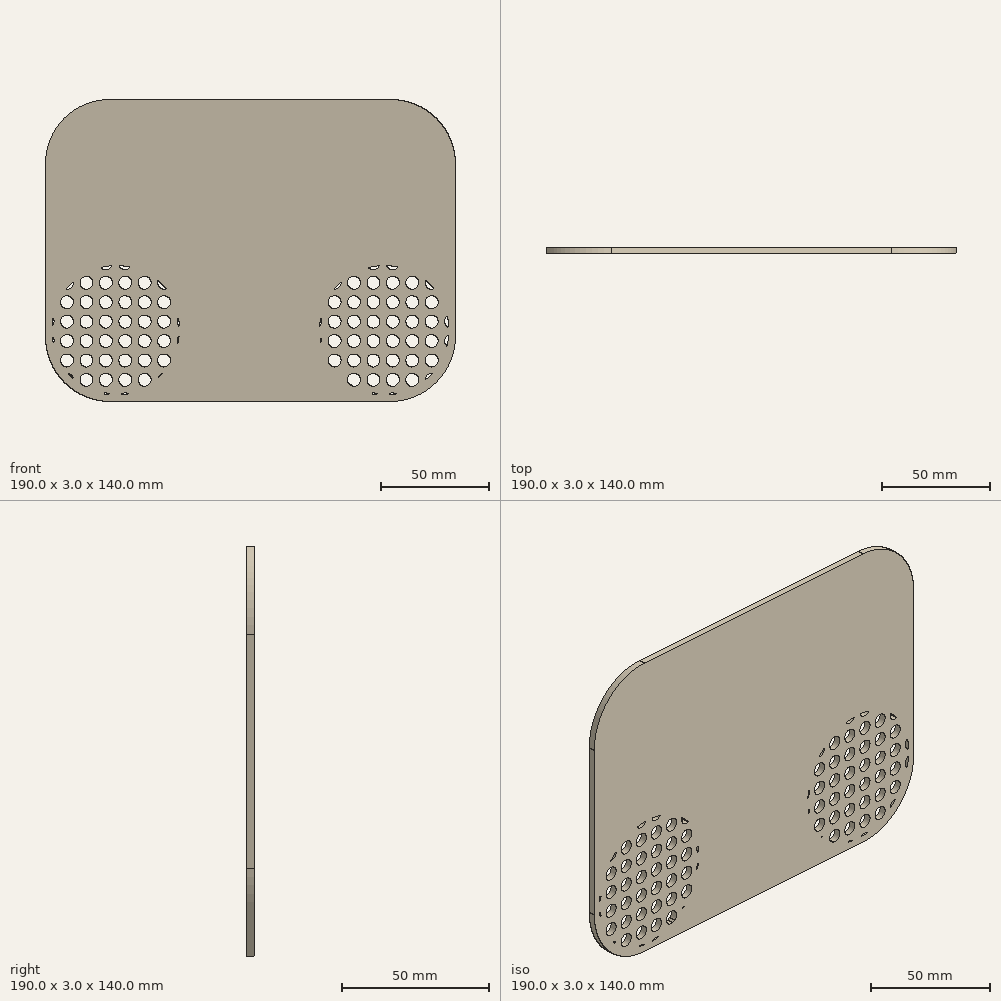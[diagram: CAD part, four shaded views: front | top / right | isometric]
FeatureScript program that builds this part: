
annotation { "Feature Type Name" : "Feature", "Feature Type Description" : "" }
export const myFeature = defineFeature(function(context is Context, id is Id, definition is map)
    precondition{}
    {
        {
            var Q0;
            Q0=qCreatedBy(makeId("Front.planeOp"),FACE);
            var sketch = newSketch(context, id + "F0", { "sketchPlane" : qUnion([Q0])});
            skArc(sketch, "E0", {"start": v(41.98, -14.66) * mm, "mid": v(40.32, -16.26) * mm, "end": v(38.79, -18) * mm});
            skArc(sketch, "E1", {"start": v(32.53, -31.39) * mm, "mid": v(32.23, -33.28) * mm, "end": v(32.05, -35.19) * mm});
            skArc(sketch, "E2", {"start": v(32.1, -39.4) * mm, "mid": v(32.32, -41.38) * mm, "end": v(32.68, -43.35) * mm});
            skArc(sketch, "E3", {"start": v(39.72, -57.09) * mm, "mid": v(40.79, -58.21) * mm, "end": v(41.91, -59.28) * mm});
            skArc(sketch, "E4", {"start": v(55.65, -66.32) * mm, "mid": v(57.37, -66.64) * mm, "end": v(59.1, -66.86) * mm});
            skArc(sketch, "E5", {"start": v(63.81, -66.95) * mm, "mid": v(65.72, -66.77) * mm, "end": v(67.61, -66.47) * mm});
            skArc(sketch, "E6", {"start": v(81, -60.21) * mm, "mid": v(82.74, -58.68) * mm, "end": v(84.34, -57.02) * mm});
            skArc(sketch, "E7", {"start": v(91.1, -44.32) * mm, "mid": v(91.62, -41.78) * mm, "end": v(91.92, -39.2) * mm});
            skArc(sketch, "E8", {"start": v(91.98, -35.82) * mm, "mid": v(91.75, -33.16) * mm, "end": v(91.3, -30.53) * mm});
            skArc(sketch, "E9", {"start": v(85.06, -17.8) * mm, "mid": v(83.21, -15.79) * mm, "end": v(81.2, -13.94) * mm});
            skArc(sketch, "E10", {"start": v(68.47, -7.7) * mm, "mid": v(65.84, -7.25) * mm, "end": v(63.18, -7.02) * mm});
            skArc(sketch, "E11", {"start": v(59.8, -7.08) * mm, "mid": v(57.22, -7.38) * mm, "end": v(54.68, -7.9) * mm});
            skLineSegment(sketch, "E12", {"start": v(-65, -70) * mm, "end": v(65, -70) * mm});
            skLineSegment(sketch, "E13", {"start": v(95, -40) * mm, "end": v(95, 40) * mm});
            skLineSegment(sketch, "E14", {"start": v(65, 70) * mm, "end": v(-65, 70) * mm});
            skLineSegment(sketch, "E15", {"start": v(-95, 40) * mm, "end": v(-95, -40) * mm});
            skArc(sketch, "E16", {"start": v(-65, 70) * mm, "mid": v(-86.21, 61.21) * mm, "end": v(-95, 40) * mm});
            skArc(sketch, "E17", {"start": v(-95, -40) * mm, "mid": v(-86.21, -61.21) * mm, "end": v(-65, -70) * mm});
            skArc(sketch, "E18", {"start": v(95, 40) * mm, "mid": v(86.21, 61.21) * mm, "end": v(65, 70) * mm});
            skArc(sketch, "E19", {"start": v(65, -70) * mm, "mid": v(86.21, -61.21) * mm, "end": v(95, -40) * mm});
            skArc(sketch, "E20", {"start": v(59.1, -66.86) * mm, "mid": v(57.46, -66.04) * mm, "end": v(55.65, -66.32) * mm});
            skArc(sketch, "E21", {"start": v(67.61, -66.47) * mm, "mid": v(65.63, -66.02) * mm, "end": v(63.81, -66.95) * mm});
            skArc(sketch, "E22", {"start": v(41.91, -59.28) * mm, "mid": v(41.12, -57.88) * mm, "end": v(39.72, -57.09) * mm});
            skCircle(sketch, "E23", {"center": v(48, -60) * mm, "radius": 3 * mm});
            skCircle(sketch, "E24", {"center": v(57, -60) * mm, "radius": 3 * mm});
            skCircle(sketch, "E25", {"center": v(66, -60) * mm, "radius": 3 * mm});
            skCircle(sketch, "E26", {"center": v(75, -60) * mm, "radius": 3 * mm});
            skArc(sketch, "E27", {"start": v(84.34, -57.02) * mm, "mid": v(81.93, -57.83) * mm, "end": v(81, -60.21) * mm});
            skCircle(sketch, "E28", {"center": v(39, -51) * mm, "radius": 3 * mm});
            skCircle(sketch, "E29", {"center": v(48, -51) * mm, "radius": 3 * mm});
            skCircle(sketch, "E30", {"center": v(57, -51) * mm, "radius": 3 * mm});
            skCircle(sketch, "E31", {"center": v(66, -51) * mm, "radius": 3 * mm});
            skCircle(sketch, "E32", {"center": v(75, -51) * mm, "radius": 3 * mm});
            skCircle(sketch, "E33", {"center": v(84, -51) * mm, "radius": 3 * mm});
            skArc(sketch, "E34", {"start": v(32.68, -43.35) * mm, "mid": v(32.96, -41.54) * mm, "end": v(32.14, -39.9) * mm});
            skCircle(sketch, "E35", {"center": v(39, -42) * mm, "radius": 3 * mm});
            skCircle(sketch, "E36", {"center": v(48, -42) * mm, "radius": 3 * mm});
            skCircle(sketch, "E37", {"center": v(57, -42) * mm, "radius": 3 * mm});
            skCircle(sketch, "E38", {"center": v(66, -42) * mm, "radius": 3 * mm});
            skCircle(sketch, "E39", {"center": v(75, -42) * mm, "radius": 3 * mm});
            skCircle(sketch, "E40", {"center": v(84, -42) * mm, "radius": 3 * mm});
            skArc(sketch, "E41", {"start": v(91.92, -39.2) * mm, "mid": v(90.04, -41.52) * mm, "end": v(91.1, -44.32) * mm});
            skArc(sketch, "E42", {"start": v(32.05, -35.19) * mm, "mid": v(32.98, -33.37) * mm, "end": v(32.53, -31.39) * mm});
            skCircle(sketch, "E43", {"center": v(39, -33) * mm, "radius": 3 * mm});
            skCircle(sketch, "E44", {"center": v(48, -33) * mm, "radius": 3 * mm});
            skCircle(sketch, "E45", {"center": v(57, -33) * mm, "radius": 3 * mm});
            skCircle(sketch, "E46", {"center": v(66, -33) * mm, "radius": 3 * mm});
            skCircle(sketch, "E47", {"center": v(75, -33) * mm, "radius": 3 * mm});
            skCircle(sketch, "E48", {"center": v(84, -33) * mm, "radius": 3 * mm});
            skArc(sketch, "E49", {"start": v(91.3, -30.53) * mm, "mid": v(90.02, -33.38) * mm, "end": v(91.98, -35.82) * mm});
            skCircle(sketch, "E50", {"center": v(39, -24) * mm, "radius": 3 * mm});
            skCircle(sketch, "E51", {"center": v(48, -24) * mm, "radius": 3 * mm});
            skCircle(sketch, "E52", {"center": v(57, -24) * mm, "radius": 3 * mm});
            skCircle(sketch, "E53", {"center": v(66, -24) * mm, "radius": 3 * mm});
            skCircle(sketch, "E54", {"center": v(75, -24) * mm, "radius": 3 * mm});
            skCircle(sketch, "E55", {"center": v(84, -24) * mm, "radius": 3 * mm});
            skArc(sketch, "E56", {"start": v(38.79, -18) * mm, "mid": v(41.17, -17.07) * mm, "end": v(41.98, -14.66) * mm});
            skCircle(sketch, "E57", {"center": v(48, -15) * mm, "radius": 3 * mm});
            skCircle(sketch, "E58", {"center": v(57, -15) * mm, "radius": 3 * mm});
            skCircle(sketch, "E59", {"center": v(66, -15) * mm, "radius": 3 * mm});
            skCircle(sketch, "E60", {"center": v(75, -15) * mm, "radius": 3 * mm});
            skArc(sketch, "E61", {"start": v(81.2, -13.94) * mm, "mid": v(81.88, -17.12) * mm, "end": v(85.06, -17.8) * mm});
            skArc(sketch, "E62", {"start": v(54.68, -7.9) * mm, "mid": v(57.48, -8.96) * mm, "end": v(59.8, -7.08) * mm});
            skArc(sketch, "E63", {"start": v(63.18, -7.02) * mm, "mid": v(65.62, -8.98) * mm, "end": v(68.47, -7.7) * mm});
            skArc(sketch, "E64", {"start": v(-84.28, -57.09) * mm, "mid": v(-83.21, -58.21) * mm, "end": v(-82.09, -59.28) * mm});
            skArc(sketch, "E65", {"start": v(-68.35, -66.32) * mm, "mid": v(-66.63, -66.64) * mm, "end": v(-64.9, -66.86) * mm});
            skArc(sketch, "E66", {"start": v(-60.19, -66.95) * mm, "mid": v(-58.28, -66.77) * mm, "end": v(-56.39, -66.47) * mm});
            skArc(sketch, "E67", {"start": v(-43.03, -60.24) * mm, "mid": v(-41.28, -58.7) * mm, "end": v(-39.66, -57.02) * mm});
            skArc(sketch, "E68", {"start": v(-32.9, -44.32) * mm, "mid": v(-32.38, -41.78) * mm, "end": v(-32.08, -39.2) * mm});
            skArc(sketch, "E69", {"start": v(-32.02, -35.82) * mm, "mid": v(-32.25, -33.16) * mm, "end": v(-32.7, -30.53) * mm});
            skArc(sketch, "E70", {"start": v(-38.94, -17.8) * mm, "mid": v(-40.79, -15.79) * mm, "end": v(-42.8, -13.94) * mm});
            skArc(sketch, "E71", {"start": v(-55.53, -7.7) * mm, "mid": v(-58.16, -7.25) * mm, "end": v(-60.82, -7.02) * mm});
            skArc(sketch, "E72", {"start": v(-64.2, -7.08) * mm, "mid": v(-66.78, -7.38) * mm, "end": v(-69.32, -7.9) * mm});
            skArc(sketch, "E73", {"start": v(-82.02, -14.66) * mm, "mid": v(-83.68, -16.26) * mm, "end": v(-85.21, -18) * mm});
            skArc(sketch, "E74", {"start": v(-91.47, -31.39) * mm, "mid": v(-91.77, -33.28) * mm, "end": v(-91.95, -35.19) * mm});
            skArc(sketch, "E75", {"start": v(-91.86, -39.9) * mm, "mid": v(-91.64, -41.63) * mm, "end": v(-91.32, -43.35) * mm});
            skArc(sketch, "E76", {"start": v(-64.9, -66.86) * mm, "mid": v(-66.54, -66.04) * mm, "end": v(-68.35, -66.32) * mm});
            skArc(sketch, "E77", {"start": v(-56.39, -66.47) * mm, "mid": v(-58.37, -66.02) * mm, "end": v(-60.19, -66.95) * mm});
            skArc(sketch, "E78", {"start": v(-82.09, -59.28) * mm, "mid": v(-82.88, -57.88) * mm, "end": v(-84.28, -57.09) * mm});
            skCircle(sketch, "E79", {"center": v(-76, -60) * mm, "radius": 3 * mm});
            skCircle(sketch, "E80", {"center": v(-67, -60) * mm, "radius": 3 * mm});
            skCircle(sketch, "E81", {"center": v(-58, -60) * mm, "radius": 3 * mm});
            skCircle(sketch, "E82", {"center": v(-49, -60) * mm, "radius": 3 * mm});
            skArc(sketch, "E83", {"start": v(-39.66, -57.02) * mm, "mid": v(-42.07, -57.83) * mm, "end": v(-43, -60.21) * mm});
            skCircle(sketch, "E84", {"center": v(-85, -51) * mm, "radius": 3 * mm});
            skCircle(sketch, "E85", {"center": v(-76, -51) * mm, "radius": 3 * mm});
            skCircle(sketch, "E86", {"center": v(-67, -51) * mm, "radius": 3 * mm});
            skCircle(sketch, "E87", {"center": v(-58, -51) * mm, "radius": 3 * mm});
            skCircle(sketch, "E88", {"center": v(-49, -51) * mm, "radius": 3 * mm});
            skCircle(sketch, "E89", {"center": v(-40, -51) * mm, "radius": 3 * mm});
            skArc(sketch, "E90", {"start": v(-91.32, -43.35) * mm, "mid": v(-91.04, -41.54) * mm, "end": v(-91.86, -39.9) * mm});
            skCircle(sketch, "E91", {"center": v(-85, -42) * mm, "radius": 3 * mm});
            skCircle(sketch, "E92", {"center": v(-76, -42) * mm, "radius": 3 * mm});
            skCircle(sketch, "E93", {"center": v(-67, -42) * mm, "radius": 3 * mm});
            skCircle(sketch, "E94", {"center": v(-58, -42) * mm, "radius": 3 * mm});
            skCircle(sketch, "E95", {"center": v(-49, -42) * mm, "radius": 3 * mm});
            skCircle(sketch, "E96", {"center": v(-40, -42) * mm, "radius": 3 * mm});
            skArc(sketch, "E97", {"start": v(-32.08, -39.2) * mm, "mid": v(-33.96, -41.52) * mm, "end": v(-32.9, -44.32) * mm});
            skArc(sketch, "E98", {"start": v(-91.95, -35.19) * mm, "mid": v(-91.02, -33.37) * mm, "end": v(-91.47, -31.39) * mm});
            skCircle(sketch, "E99", {"center": v(-85, -33) * mm, "radius": 3 * mm});
            skCircle(sketch, "E100", {"center": v(-76, -33) * mm, "radius": 3 * mm});
            skCircle(sketch, "E101", {"center": v(-67, -33) * mm, "radius": 3 * mm});
            skCircle(sketch, "E102", {"center": v(-58, -33) * mm, "radius": 3 * mm});
            skCircle(sketch, "E103", {"center": v(-49, -33) * mm, "radius": 3 * mm});
            skCircle(sketch, "E104", {"center": v(-40, -33) * mm, "radius": 3 * mm});
            skArc(sketch, "E105", {"start": v(-32.7, -30.53) * mm, "mid": v(-33.98, -33.38) * mm, "end": v(-32.02, -35.82) * mm});
            skCircle(sketch, "E106", {"center": v(-85, -24) * mm, "radius": 3 * mm});
            skCircle(sketch, "E107", {"center": v(-76, -24) * mm, "radius": 3 * mm});
            skCircle(sketch, "E108", {"center": v(-67, -24) * mm, "radius": 3 * mm});
            skCircle(sketch, "E109", {"center": v(-58, -24) * mm, "radius": 3 * mm});
            skCircle(sketch, "E110", {"center": v(-49, -24) * mm, "radius": 3 * mm});
            skCircle(sketch, "E111", {"center": v(-40, -24) * mm, "radius": 3 * mm});
            skArc(sketch, "E112", {"start": v(-85.21, -18) * mm, "mid": v(-82.83, -17.07) * mm, "end": v(-82.02, -14.66) * mm});
            skCircle(sketch, "E113", {"center": v(-76, -15) * mm, "radius": 3 * mm});
            skCircle(sketch, "E114", {"center": v(-67, -15) * mm, "radius": 3 * mm});
            skCircle(sketch, "E115", {"center": v(-58, -15) * mm, "radius": 3 * mm});
            skCircle(sketch, "E116", {"center": v(-49, -15) * mm, "radius": 3 * mm});
            skArc(sketch, "E117", {"start": v(-42.8, -13.94) * mm, "mid": v(-42.12, -17.12) * mm, "end": v(-38.94, -17.8) * mm});
            skArc(sketch, "E118", {"start": v(-69.32, -7.9) * mm, "mid": v(-66.52, -8.96) * mm, "end": v(-64.2, -7.08) * mm});
            skArc(sketch, "E119", {"start": v(-60.82, -7.02) * mm, "mid": v(-58.38, -8.98) * mm, "end": v(-55.53, -7.7) * mm});
            skSolve(sketch);
        }
        {
            var Q0;
            Q0 = qSketchRegion(id + "F0", true);
            extrude(context, id + "F1", {"entities" : qUnion([Q0]), "depth" : 3 * mm});
        }
        {
            var Q0;
            Q0=makeQuery(id+"F1.opExtrude","CAP_FACE",FACE,{"disambiguationData":[OSD([sQuery(id+"F0.wireOp",EDGE,"E0"),sQuery(id+"F0.wireOp",EDGE,"E1"),sQuery(id+"F0.wireOp",EDGE,"E2"),sQuery(id+"F0.wireOp",EDGE,"E3"),sQuery(id+"F0.wireOp",EDGE,"E4"),sQuery(id+"F0.wireOp",EDGE,"E5"),sQuery(id+"F0.wireOp",EDGE,"E6"),sQuery(id+"F0.wireOp",EDGE,"E7"),sQuery(id+"F0.wireOp",EDGE,"E8"),sQuery(id+"F0.wireOp",EDGE,"E9"),sQuery(id+"F0.wireOp",EDGE,"E10"),sQuery(id+"F0.wireOp",EDGE,"E11"),sQuery(id+"F0.wireOp",EDGE,"E12"),sQuery(id+"F0.wireOp",EDGE,"E13"),sQuery(id+"F0.wireOp",EDGE,"E14"),sQuery(id+"F0.wireOp",EDGE,"E15"),sQuery(id+"F0.wireOp",EDGE,"E16"),sQuery(id+"F0.wireOp",EDGE,"E17"),sQuery(id+"F0.wireOp",EDGE,"E18"),sQuery(id+"F0.wireOp",EDGE,"E19"),sQuery(id+"F0.wireOp",EDGE,"E20"),sQuery(id+"F0.wireOp",EDGE,"E21"),sQuery(id+"F0.wireOp",EDGE,"E22"),sQuery(id+"F0.wireOp",EDGE,"E23"),sQuery(id+"F0.wireOp",EDGE,"E24"),sQuery(id+"F0.wireOp",EDGE,"E25"),sQuery(id+"F0.wireOp",EDGE,"E26"),sQuery(id+"F0.wireOp",EDGE,"E27"),sQuery(id+"F0.wireOp",EDGE,"E28"),sQuery(id+"F0.wireOp",EDGE,"E29"),sQuery(id+"F0.wireOp",EDGE,"E30"),sQuery(id+"F0.wireOp",EDGE,"E31"),sQuery(id+"F0.wireOp",EDGE,"E32"),sQuery(id+"F0.wireOp",EDGE,"E33"),sQuery(id+"F0.wireOp",EDGE,"E34"),sQuery(id+"F0.wireOp",EDGE,"E35"),sQuery(id+"F0.wireOp",EDGE,"E36"),sQuery(id+"F0.wireOp",EDGE,"E37"),sQuery(id+"F0.wireOp",EDGE,"E38"),sQuery(id+"F0.wireOp",EDGE,"E39"),sQuery(id+"F0.wireOp",EDGE,"E40"),sQuery(id+"F0.wireOp",EDGE,"E41"),sQuery(id+"F0.wireOp",EDGE,"E42"),sQuery(id+"F0.wireOp",EDGE,"E43"),sQuery(id+"F0.wireOp",EDGE,"E44"),sQuery(id+"F0.wireOp",EDGE,"E45"),sQuery(id+"F0.wireOp",EDGE,"E46"),sQuery(id+"F0.wireOp",EDGE,"E47"),sQuery(id+"F0.wireOp",EDGE,"E48"),sQuery(id+"F0.wireOp",EDGE,"E49"),sQuery(id+"F0.wireOp",EDGE,"E50"),sQuery(id+"F0.wireOp",EDGE,"E51"),sQuery(id+"F0.wireOp",EDGE,"E52"),sQuery(id+"F0.wireOp",EDGE,"E53"),sQuery(id+"F0.wireOp",EDGE,"E54"),sQuery(id+"F0.wireOp",EDGE,"E55"),sQuery(id+"F0.wireOp",EDGE,"E56"),sQuery(id+"F0.wireOp",EDGE,"E57"),sQuery(id+"F0.wireOp",EDGE,"E58"),sQuery(id+"F0.wireOp",EDGE,"E59"),sQuery(id+"F0.wireOp",EDGE,"E60"),sQuery(id+"F0.wireOp",EDGE,"E61"),sQuery(id+"F0.wireOp",EDGE,"E62"),sQuery(id+"F0.wireOp",EDGE,"E63"),sQuery(id+"F0.wireOp",EDGE,"E64"),sQuery(id+"F0.wireOp",EDGE,"E65"),sQuery(id+"F0.wireOp",EDGE,"E66"),sQuery(id+"F0.wireOp",EDGE,"E67"),sQuery(id+"F0.wireOp",EDGE,"E68"),sQuery(id+"F0.wireOp",EDGE,"E69"),sQuery(id+"F0.wireOp",EDGE,"E70"),sQuery(id+"F0.wireOp",EDGE,"E71"),sQuery(id+"F0.wireOp",EDGE,"E72"),sQuery(id+"F0.wireOp",EDGE,"E73"),sQuery(id+"F0.wireOp",EDGE,"E74"),sQuery(id+"F0.wireOp",EDGE,"E75"),sQuery(id+"F0.wireOp",EDGE,"E76"),sQuery(id+"F0.wireOp",EDGE,"E77"),sQuery(id+"F0.wireOp",EDGE,"E78"),sQuery(id+"F0.wireOp",EDGE,"E79"),sQuery(id+"F0.wireOp",EDGE,"E80"),sQuery(id+"F0.wireOp",EDGE,"E81"),sQuery(id+"F0.wireOp",EDGE,"E82"),sQuery(id+"F0.wireOp",EDGE,"E83"),sQuery(id+"F0.wireOp",EDGE,"E84"),sQuery(id+"F0.wireOp",EDGE,"E85"),sQuery(id+"F0.wireOp",EDGE,"E86"),sQuery(id+"F0.wireOp",EDGE,"E87"),sQuery(id+"F0.wireOp",EDGE,"E88"),sQuery(id+"F0.wireOp",EDGE,"E89"),sQuery(id+"F0.wireOp",EDGE,"E90"),sQuery(id+"F0.wireOp",EDGE,"E91"),sQuery(id+"F0.wireOp",EDGE,"E92"),sQuery(id+"F0.wireOp",EDGE,"E93"),sQuery(id+"F0.wireOp",EDGE,"E94"),sQuery(id+"F0.wireOp",EDGE,"E95"),sQuery(id+"F0.wireOp",EDGE,"E96"),sQuery(id+"F0.wireOp",EDGE,"E97"),sQuery(id+"F0.wireOp",EDGE,"E98"),sQuery(id+"F0.wireOp",EDGE,"E99"),sQuery(id+"F0.wireOp",EDGE,"E100"),sQuery(id+"F0.wireOp",EDGE,"E101"),sQuery(id+"F0.wireOp",EDGE,"E102"),sQuery(id+"F0.wireOp",EDGE,"E103"),sQuery(id+"F0.wireOp",EDGE,"E104"),sQuery(id+"F0.wireOp",EDGE,"E105"),sQuery(id+"F0.wireOp",EDGE,"E106"),sQuery(id+"F0.wireOp",EDGE,"E107"),sQuery(id+"F0.wireOp",EDGE,"E108"),sQuery(id+"F0.wireOp",EDGE,"E109"),sQuery(id+"F0.wireOp",EDGE,"E110"),sQuery(id+"F0.wireOp",EDGE,"E111"),sQuery(id+"F0.wireOp",EDGE,"E112"),sQuery(id+"F0.wireOp",EDGE,"E113"),sQuery(id+"F0.wireOp",EDGE,"E114"),sQuery(id+"F0.wireOp",EDGE,"E115"),sQuery(id+"F0.wireOp",EDGE,"E116"),sQuery(id+"F0.wireOp",EDGE,"E117"),sQuery(id+"F0.wireOp",EDGE,"E118"),sQuery(id+"F0.wireOp",EDGE,"E119")])],"isStart":false});
            var sketch = newSketch(context, id + "F2", { "sketchPlane" : qUnion([Q0])});
            skLineSegment(sketch, "E120", {"start": v(77.02, 48) * mm, "end": v(77.02, -10.74) * mm});
            skArc(sketch, "E121", {"start": v(77.02, -10.74) * mm, "mid": v(35.92, -21.87) * mm, "end": v(47.46, -62.85) * mm});
            skLineSegment(sketch, "E122", {"start": v(-48.07, -62.85) * mm, "end": v(47.46, -62.85) * mm});
            skArc(sketch, "E123", {"start": v(-48.07, -62.85) * mm, "mid": v(-34.84, -47.38) * mm, "end": v(-34.5, -27.03) * mm});
            skPoint(sketch, "E124.end.orphan", {"position": v(-31, -33) * mm});
            skLineSegment(sketch, "E125", {"start": v(72.26, 50.43) * mm, "end": v(-34.5, -27.03) * mm});
            skPoint(sketch, "E126.visualSharp", {"position": v(77.02, 53.88) * mm});
            skArc(sketch, "E126.filletArc", {"start": v(77.02, 48) * mm, "mid": v(75.38, 50.67) * mm, "end": v(72.26, 50.43) * mm});
            skSolve(sketch);
        }
        {
            var Q0;
            Q0 = qSketchRegion(id + "F2", true);
            extrude(context, id + "F3", {"entities" : qUnion([Q0]), "operationType" : NewBodyOperationType.ADD, "oppositeDirection" : true, "depth" : 3 * mm});
        }
        {
            var Q0;
            Q0=makeQuery(id+"F1.opExtrude","CAP_FACE",FACE,{"disambiguationData":[OSD([sQuery(id+"F0.wireOp",EDGE,"E0"),sQuery(id+"F0.wireOp",EDGE,"E1"),sQuery(id+"F0.wireOp",EDGE,"E2"),sQuery(id+"F0.wireOp",EDGE,"E3"),sQuery(id+"F0.wireOp",EDGE,"E4"),sQuery(id+"F0.wireOp",EDGE,"E5"),sQuery(id+"F0.wireOp",EDGE,"E6"),sQuery(id+"F0.wireOp",EDGE,"E7"),sQuery(id+"F0.wireOp",EDGE,"E8"),sQuery(id+"F0.wireOp",EDGE,"E9"),sQuery(id+"F0.wireOp",EDGE,"E10"),sQuery(id+"F0.wireOp",EDGE,"E11"),sQuery(id+"F0.wireOp",EDGE,"E12"),sQuery(id+"F0.wireOp",EDGE,"E13"),sQuery(id+"F0.wireOp",EDGE,"E14"),sQuery(id+"F0.wireOp",EDGE,"E15"),sQuery(id+"F0.wireOp",EDGE,"E16"),sQuery(id+"F0.wireOp",EDGE,"E17"),sQuery(id+"F0.wireOp",EDGE,"E18"),sQuery(id+"F0.wireOp",EDGE,"E19"),sQuery(id+"F0.wireOp",EDGE,"E20"),sQuery(id+"F0.wireOp",EDGE,"E21"),sQuery(id+"F0.wireOp",EDGE,"E22"),sQuery(id+"F0.wireOp",EDGE,"E23"),sQuery(id+"F0.wireOp",EDGE,"E24"),sQuery(id+"F0.wireOp",EDGE,"E25"),sQuery(id+"F0.wireOp",EDGE,"E26"),sQuery(id+"F0.wireOp",EDGE,"E27"),sQuery(id+"F0.wireOp",EDGE,"E28"),sQuery(id+"F0.wireOp",EDGE,"E29"),sQuery(id+"F0.wireOp",EDGE,"E30"),sQuery(id+"F0.wireOp",EDGE,"E31"),sQuery(id+"F0.wireOp",EDGE,"E32"),sQuery(id+"F0.wireOp",EDGE,"E33"),sQuery(id+"F0.wireOp",EDGE,"E34"),sQuery(id+"F0.wireOp",EDGE,"E35"),sQuery(id+"F0.wireOp",EDGE,"E36"),sQuery(id+"F0.wireOp",EDGE,"E37"),sQuery(id+"F0.wireOp",EDGE,"E38"),sQuery(id+"F0.wireOp",EDGE,"E39"),sQuery(id+"F0.wireOp",EDGE,"E40"),sQuery(id+"F0.wireOp",EDGE,"E41"),sQuery(id+"F0.wireOp",EDGE,"E42"),sQuery(id+"F0.wireOp",EDGE,"E43"),sQuery(id+"F0.wireOp",EDGE,"E44"),sQuery(id+"F0.wireOp",EDGE,"E45"),sQuery(id+"F0.wireOp",EDGE,"E46"),sQuery(id+"F0.wireOp",EDGE,"E47"),sQuery(id+"F0.wireOp",EDGE,"E48"),sQuery(id+"F0.wireOp",EDGE,"E49"),sQuery(id+"F0.wireOp",EDGE,"E50"),sQuery(id+"F0.wireOp",EDGE,"E51"),sQuery(id+"F0.wireOp",EDGE,"E52"),sQuery(id+"F0.wireOp",EDGE,"E53"),sQuery(id+"F0.wireOp",EDGE,"E54"),sQuery(id+"F0.wireOp",EDGE,"E55"),sQuery(id+"F0.wireOp",EDGE,"E56"),sQuery(id+"F0.wireOp",EDGE,"E57"),sQuery(id+"F0.wireOp",EDGE,"E58"),sQuery(id+"F0.wireOp",EDGE,"E59"),sQuery(id+"F0.wireOp",EDGE,"E60"),sQuery(id+"F0.wireOp",EDGE,"E61"),sQuery(id+"F0.wireOp",EDGE,"E62"),sQuery(id+"F0.wireOp",EDGE,"E63"),sQuery(id+"F0.wireOp",EDGE,"E64"),sQuery(id+"F0.wireOp",EDGE,"E65"),sQuery(id+"F0.wireOp",EDGE,"E66"),sQuery(id+"F0.wireOp",EDGE,"E67"),sQuery(id+"F0.wireOp",EDGE,"E68"),sQuery(id+"F0.wireOp",EDGE,"E69"),sQuery(id+"F0.wireOp",EDGE,"E70"),sQuery(id+"F0.wireOp",EDGE,"E71"),sQuery(id+"F0.wireOp",EDGE,"E72"),sQuery(id+"F0.wireOp",EDGE,"E73"),sQuery(id+"F0.wireOp",EDGE,"E74"),sQuery(id+"F0.wireOp",EDGE,"E75"),sQuery(id+"F0.wireOp",EDGE,"E76"),sQuery(id+"F0.wireOp",EDGE,"E77"),sQuery(id+"F0.wireOp",EDGE,"E78"),sQuery(id+"F0.wireOp",EDGE,"E79"),sQuery(id+"F0.wireOp",EDGE,"E80"),sQuery(id+"F0.wireOp",EDGE,"E81"),sQuery(id+"F0.wireOp",EDGE,"E82"),sQuery(id+"F0.wireOp",EDGE,"E83"),sQuery(id+"F0.wireOp",EDGE,"E84"),sQuery(id+"F0.wireOp",EDGE,"E85"),sQuery(id+"F0.wireOp",EDGE,"E86"),sQuery(id+"F0.wireOp",EDGE,"E87"),sQuery(id+"F0.wireOp",EDGE,"E88"),sQuery(id+"F0.wireOp",EDGE,"E89"),sQuery(id+"F0.wireOp",EDGE,"E90"),sQuery(id+"F0.wireOp",EDGE,"E91"),sQuery(id+"F0.wireOp",EDGE,"E92"),sQuery(id+"F0.wireOp",EDGE,"E93"),sQuery(id+"F0.wireOp",EDGE,"E94"),sQuery(id+"F0.wireOp",EDGE,"E95"),sQuery(id+"F0.wireOp",EDGE,"E96"),sQuery(id+"F0.wireOp",EDGE,"E97"),sQuery(id+"F0.wireOp",EDGE,"E98"),sQuery(id+"F0.wireOp",EDGE,"E99"),sQuery(id+"F0.wireOp",EDGE,"E100"),sQuery(id+"F0.wireOp",EDGE,"E101"),sQuery(id+"F0.wireOp",EDGE,"E102"),sQuery(id+"F0.wireOp",EDGE,"E103"),sQuery(id+"F0.wireOp",EDGE,"E104"),sQuery(id+"F0.wireOp",EDGE,"E105"),sQuery(id+"F0.wireOp",EDGE,"E106"),sQuery(id+"F0.wireOp",EDGE,"E107"),sQuery(id+"F0.wireOp",EDGE,"E108"),sQuery(id+"F0.wireOp",EDGE,"E109"),sQuery(id+"F0.wireOp",EDGE,"E110"),sQuery(id+"F0.wireOp",EDGE,"E111"),sQuery(id+"F0.wireOp",EDGE,"E112"),sQuery(id+"F0.wireOp",EDGE,"E113"),sQuery(id+"F0.wireOp",EDGE,"E114"),sQuery(id+"F0.wireOp",EDGE,"E115"),sQuery(id+"F0.wireOp",EDGE,"E116"),sQuery(id+"F0.wireOp",EDGE,"E117"),sQuery(id+"F0.wireOp",EDGE,"E118"),sQuery(id+"F0.wireOp",EDGE,"E119")])],"isStart":false});
            var sketch = newSketch(context, id + "F4", { "sketchPlane" : qUnion([Q0])});
            skLineSegment(sketch, "E127", {"start": v(-64.2, -6.93) * mm, "end": v(-64.2, -7.08) * mm});
            skPoint(sketch, "E128.center.orphan", {"position": v(-62, -37) * mm});
            skPoint(sketch, "E128.end.orphan", {"position": v(-40.79, -15.79) * mm});
            skLineSegment(sketch, "E129", {"start": v(-78.35, 53.66) * mm, "end": v(-78.35, -13.14) * mm});
            skLineSegment(sketch, "E130", {"start": v(-73.27, 55.82) * mm, "end": v(-17.78, 2.44) * mm});
            skLineSegment(sketch, "E131", {"start": v(-18.06, -2.12) * mm, "end": v(-38.94, -17.8) * mm});
            skFitSpline(sketch, "E132", {"points": [v(-78.35, -13.14) * mm, v(-69.32, -7.9) * mm, v(-55.53, -7.7) * mm, v(-42.8, -13.94) * mm, v(-38.94, -17.8) * mm], "startDerivative": vector(29.94, 21.25) * mm, "endDerivative": vector(16.98, -20.17) * mm});
            skPoint(sketch, "E133.visualSharp", {"position": v(-15.24, 0) * mm});
            skArc(sketch, "E133.filletArc", {"start": v(-18.06, -2.12) * mm, "mid": v(-16.87, 0.1) * mm, "end": v(-17.78, 2.44) * mm});
            skPoint(sketch, "E134.visualSharp", {"position": v(-78.35, 60.7) * mm});
            skArc(sketch, "E134.filletArc", {"start": v(-73.27, 55.82) * mm, "mid": v(-76.53, 56.42) * mm, "end": v(-78.35, 53.66) * mm});
            skSolve(sketch);
        }
        {
            var Q0;
            Q0 = qSketchRegion(id + "F4", true);
            extrude(context, id + "F5", {"entities" : qUnion([Q0]), "operationType" : NewBodyOperationType.ADD, "oppositeDirection" : true, "depth" : 3 * mm});
        }
    });
